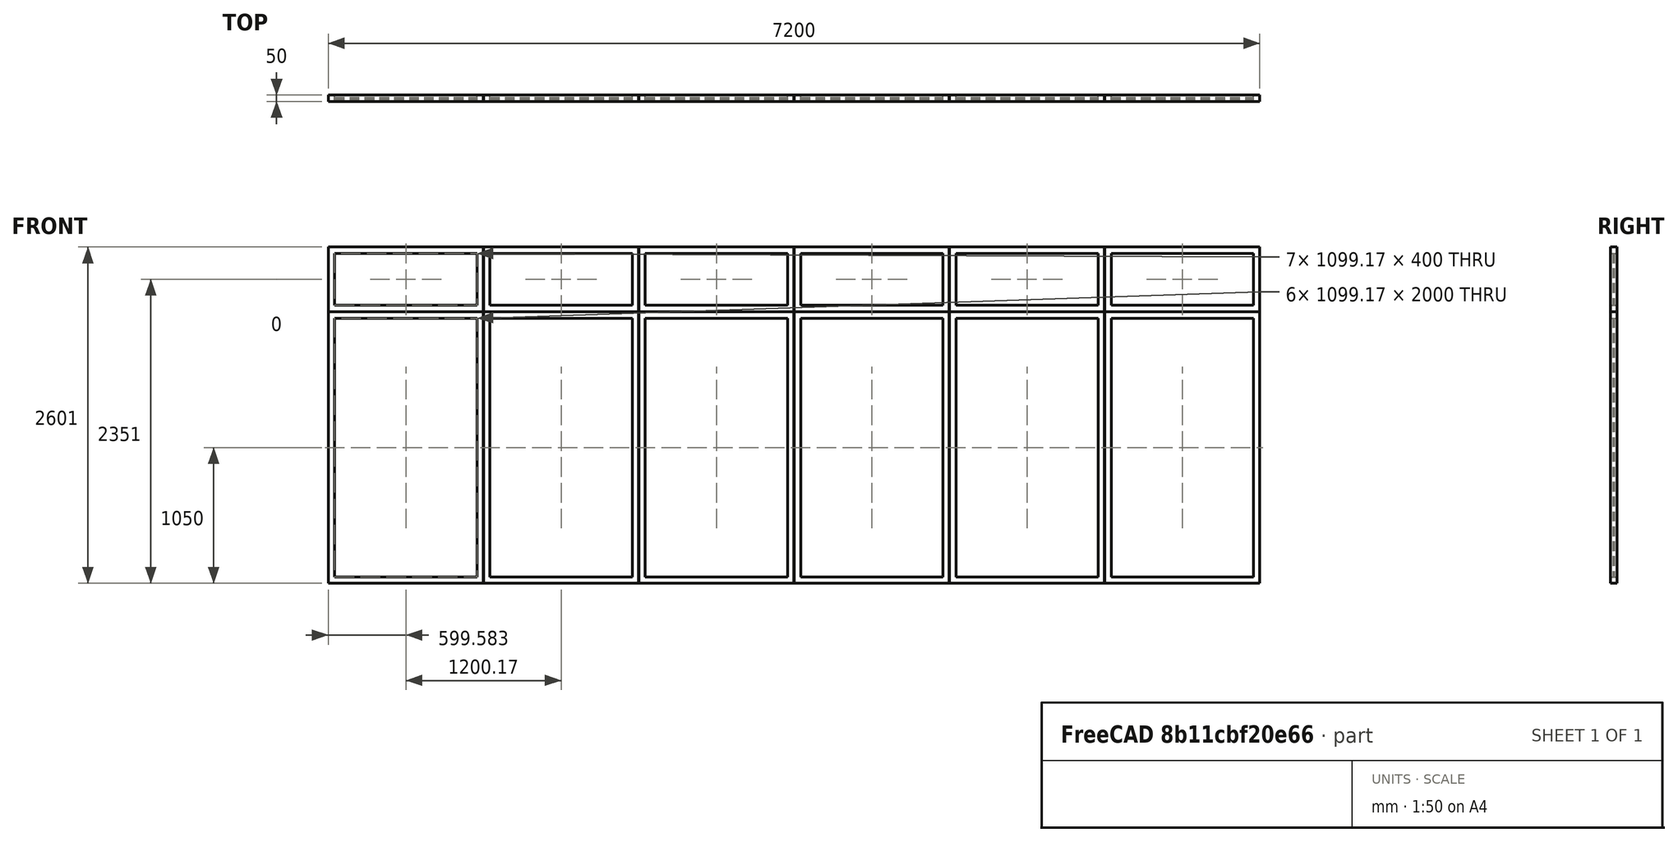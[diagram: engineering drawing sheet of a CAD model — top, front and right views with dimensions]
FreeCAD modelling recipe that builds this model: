
FCSTD DOCUMENT  (FreeCAD 0.16R6704 (Git))
Label: 6 frame modules
License: CreativeCommons Attribution
LicenseURL: http://creativecommons.org/licenses/by/4.0/
objects: Sketcher::SketchObject×1, Part::FeaturePython×1
note: 2 computed .brp shape members not serialized (recipe doc carries the construction recipe); baked Part::Feature solids carry a one-line shape summary decoded from their .brp

FEATURE [Sketcher::SketchObject] Sketch189
  Placement = pos=(0,0,0) rot=(1,0,0;1.5708rad)
  sketch-geometry (125):
    g0: LineSegment StartX=-2 StartY=-2 StartZ=0 EndX=7202 EndY=-2 EndZ=0
    g1: LineSegment StartX=7202 StartY=-2 StartZ=0 EndX=7202 EndY=2603 EndZ=0
    g2: LineSegment StartX=7202 StartY=2603 StartZ=0 EndX=-2 EndY=2603 EndZ=0
    g3: LineSegment StartX=-2 StartY=2603 StartZ=0 EndX=-2 EndY=-2 EndZ=0
    g4: LineSegment StartX=0 StartY=2601 StartZ=0 EndX=1199.17 EndY=2601 EndZ=0
    g5: LineSegment StartX=1199.17 StartY=2601 StartZ=0 EndX=1199.17 EndY=2101 EndZ=0
    g6: LineSegment StartX=1199.17 StartY=2101 StartZ=0 EndX=0 EndY=2101 EndZ=0
    g7: LineSegment StartX=0 StartY=2101 StartZ=0 EndX=0 EndY=2601 EndZ=0
    g8: LineSegment StartX=50 StartY=2551 StartZ=0 EndX=1149.17 EndY=2551 EndZ=0
    g9: LineSegment StartX=1149.17 StartY=2551 StartZ=0 EndX=1149.17 EndY=2151 EndZ=0
    g10: LineSegment StartX=1149.17 StartY=2151 StartZ=0 EndX=50 EndY=2151 EndZ=0
    g11: LineSegment StartX=50 StartY=2151 StartZ=0 EndX=50 EndY=2551 EndZ=0
    g12: LineSegment StartX=0 StartY=2100 StartZ=0 EndX=1199.17 EndY=2100 EndZ=0
    g13: LineSegment StartX=1199.17 StartY=2100 StartZ=0 EndX=1199.17 EndY=0 EndZ=0
    g14: LineSegment StartX=1199.17 StartY=0 StartZ=0 EndX=0 EndY=0 EndZ=0
    g15: LineSegment StartX=0 StartY=0 StartZ=0 EndX=0 EndY=2100 EndZ=0
    g16: LineSegment StartX=50 StartY=2050 StartZ=0 EndX=1149.17 EndY=2050 EndZ=0
    g17: LineSegment StartX=1149.17 StartY=2050 StartZ=0 EndX=1149.17 EndY=50 EndZ=0
    g18: LineSegment StartX=1149.17 StartY=50 StartZ=0 EndX=50 EndY=50 EndZ=0
    g19: LineSegment StartX=50 StartY=50 StartZ=0 EndX=50 EndY=2050 EndZ=0
    g20: LineSegment StartX=-1 StartY=2602 StartZ=0 EndX=7201 EndY=2602 EndZ=0
    g21: LineSegment StartX=7201 StartY=2602 StartZ=0 EndX=7201 EndY=-1 EndZ=0
    g22: LineSegment StartX=7201 StartY=-1 StartZ=0 EndX=-1 EndY=-1 EndZ=0
    g23: LineSegment StartX=-1 StartY=-1 StartZ=0 EndX=-1 EndY=2602 EndZ=0
    g24: LineSegment StartX=1200.17 StartY=2601 StartZ=0 EndX=2399.33 EndY=2601 EndZ=0
    g25: LineSegment StartX=2399.33 StartY=2601 StartZ=0 EndX=2399.33 EndY=2101 EndZ=0
    g26: LineSegment StartX=2399.33 StartY=2101 StartZ=0 EndX=1200.17 EndY=2101 EndZ=0
    g27: LineSegment StartX=1200.17 StartY=2101 StartZ=0 EndX=1200.17 EndY=2601 EndZ=0
    g28: LineSegment StartX=1250.17 StartY=2551 StartZ=0 EndX=2349.33 EndY=2551 EndZ=0
    g29: LineSegment StartX=2349.33 StartY=2551 StartZ=0 EndX=2349.33 EndY=2151 EndZ=0
    g30: LineSegment StartX=2349.33 StartY=2151 StartZ=0 EndX=1250.17 EndY=2151 EndZ=0
    g31: LineSegment StartX=1250.17 StartY=2151 StartZ=0 EndX=1250.17 EndY=2551 EndZ=0
    g32: LineSegment StartX=1200.17 StartY=2100 StartZ=0 EndX=2399.33 EndY=2100 EndZ=0
    g33: LineSegment StartX=2399.33 StartY=2100 StartZ=0 EndX=2399.33 EndY=0 EndZ=0
    g34: LineSegment StartX=2399.33 StartY=0 StartZ=0 EndX=1200.17 EndY=0 EndZ=0
    g35: LineSegment StartX=1200.17 StartY=0 StartZ=0 EndX=1200.17 EndY=2100 EndZ=0
    g36: LineSegment StartX=1250.17 StartY=2050 StartZ=0 EndX=2349.33 EndY=2050 EndZ=0
    g37: LineSegment StartX=2349.33 StartY=2050 StartZ=0 EndX=2349.33 EndY=50 EndZ=0
    g38: LineSegment StartX=2349.33 StartY=50 StartZ=0 EndX=1250.17 EndY=50 EndZ=0
    g39: LineSegment StartX=1250.17 StartY=50 StartZ=0 EndX=1250.17 EndY=2050 EndZ=0
    g40: LineSegment [constr] StartX=0 StartY=2601 StartZ=0 EndX=1200.17 EndY=2601 EndZ=0
    g41: LineSegment StartX=2400.33 StartY=2601 StartZ=0 EndX=3599.5 EndY=2601 EndZ=0
    g42: LineSegment StartX=3599.5 StartY=2601 StartZ=0 EndX=3599.5 EndY=2101 EndZ=0
    g43: LineSegment StartX=3599.5 StartY=2101 StartZ=0 EndX=2400.33 EndY=2101 EndZ=0
    g44: LineSegment StartX=2400.33 StartY=2101 StartZ=0 EndX=2400.33 EndY=2601 EndZ=0
    g45: LineSegment StartX=2450.33 StartY=2551 StartZ=0 EndX=3549.5 EndY=2551 EndZ=0
    g46: LineSegment StartX=3549.5 StartY=2551 StartZ=0 EndX=3549.5 EndY=2151 EndZ=0
    g47: LineSegment StartX=3549.5 StartY=2151 StartZ=0 EndX=2450.33 EndY=2151 EndZ=0
    g48: LineSegment StartX=2450.33 StartY=2151 StartZ=0 EndX=2450.33 EndY=2551 EndZ=0
    g49: LineSegment StartX=2400.33 StartY=2100 StartZ=0 EndX=3599.5 EndY=2100 EndZ=0
    g50: LineSegment StartX=3599.5 StartY=2100 StartZ=0 EndX=3599.5 EndY=0 EndZ=0
    g51: LineSegment StartX=3599.5 StartY=0 StartZ=0 EndX=2400.33 EndY=0 EndZ=0
    g52: LineSegment StartX=2400.33 StartY=0 StartZ=0 EndX=2400.33 EndY=2100 EndZ=0
    g53: LineSegment StartX=2450.33 StartY=2050 StartZ=0 EndX=3549.5 EndY=2050 EndZ=0
    g54: LineSegment StartX=3549.5 StartY=2050 StartZ=0 EndX=3549.5 EndY=50 EndZ=0
    g55: LineSegment StartX=3549.5 StartY=50 StartZ=0 EndX=2450.33 EndY=50 EndZ=0
    g56: LineSegment StartX=2450.33 StartY=50 StartZ=0 EndX=2450.33 EndY=2050 EndZ=0
    g57: LineSegment [constr] StartX=1200.17 StartY=2601 StartZ=0 EndX=2400.33 EndY=2601 EndZ=0
    g58: LineSegment StartX=3600.5 StartY=2601 StartZ=0 EndX=4799.67 EndY=2601 EndZ=0
    g59: LineSegment StartX=4799.67 StartY=2601 StartZ=0 EndX=4799.67 EndY=2101 EndZ=0
    g60: LineSegment StartX=4799.67 StartY=2101 StartZ=0 EndX=3600.5 EndY=2101 EndZ=0
    g61: LineSegment StartX=3600.5 StartY=2101 StartZ=0 EndX=3600.5 EndY=2601 EndZ=0
    g62: LineSegment StartX=3650.5 StartY=2551 StartZ=0 EndX=4749.67 EndY=2551 EndZ=0
    g63: LineSegment StartX=4749.67 StartY=2551 StartZ=0 EndX=4749.67 EndY=2151 EndZ=0
    g64: LineSegment StartX=4749.67 StartY=2151 StartZ=0 EndX=3650.5 EndY=2151 EndZ=0
    g65: LineSegment StartX=3650.5 StartY=2151 StartZ=0 EndX=3650.5 EndY=2551 EndZ=0
    g66: LineSegment StartX=3600.5 StartY=2100 StartZ=0 EndX=4799.67 EndY=2100 EndZ=0
    g67: LineSegment StartX=4799.67 StartY=2100 StartZ=0 EndX=4799.67 EndY=0 EndZ=0
    g68: LineSegment StartX=4799.67 StartY=0 StartZ=0 EndX=3600.5 EndY=0 EndZ=0
    g69: LineSegment StartX=3600.5 StartY=0 StartZ=0 EndX=3600.5 EndY=2100 EndZ=0
    g70: LineSegment StartX=3650.5 StartY=2050 StartZ=0 EndX=4749.67 EndY=2050 EndZ=0
    g71: LineSegment StartX=4749.67 StartY=2050 StartZ=0 EndX=4749.67 EndY=50 EndZ=0
    g72: LineSegment StartX=4749.67 StartY=50 StartZ=0 EndX=3650.5 EndY=50 EndZ=0
    g73: LineSegment StartX=3650.5 StartY=50 StartZ=0 EndX=3650.5 EndY=2050 EndZ=0
    g74: LineSegment [constr] StartX=2400.33 StartY=2601 StartZ=0 EndX=3600.5 EndY=2601 EndZ=0
    g75: LineSegment StartX=4800.67 StartY=2601 StartZ=0 EndX=5999.83 EndY=2601 EndZ=0
    g76: LineSegment StartX=5999.83 StartY=2601 StartZ=0 EndX=5999.83 EndY=2101 EndZ=0
    g77: LineSegment StartX=5999.83 StartY=2101 StartZ=0 EndX=4800.67 EndY=2101 EndZ=0
    g78: LineSegment StartX=4800.67 StartY=2101 StartZ=0 EndX=4800.67 EndY=2601 EndZ=0
    g79: LineSegment StartX=4850.67 StartY=2551 StartZ=0 EndX=5949.83 EndY=2551 EndZ=0
    g80: LineSegment StartX=5949.83 StartY=2551 StartZ=0 EndX=5949.83 EndY=2151 EndZ=0
    g81: LineSegment StartX=5949.83 StartY=2151 StartZ=0 EndX=4850.67 EndY=2151 EndZ=0
    g82: LineSegment StartX=4850.67 StartY=2151 StartZ=0 EndX=4850.67 EndY=2551 EndZ=0
    g83: LineSegment StartX=4800.67 StartY=2100 StartZ=0 EndX=5999.83 EndY=2100 EndZ=0
    g84: LineSegment StartX=5999.83 StartY=2100 StartZ=0 EndX=5999.83 EndY=0 EndZ=0
    g85: LineSegment StartX=5999.83 StartY=0 StartZ=0 EndX=4800.67 EndY=0 EndZ=0
    g86: LineSegment StartX=4800.67 StartY=0 StartZ=0 EndX=4800.67 EndY=2100 EndZ=0
    g87: LineSegment StartX=4850.67 StartY=2050 StartZ=0 EndX=5949.83 EndY=2050 EndZ=0
    g88: LineSegment StartX=5949.83 StartY=2050 StartZ=0 EndX=5949.83 EndY=50 EndZ=0
    g89: LineSegment StartX=5949.83 StartY=50 StartZ=0 EndX=4850.67 EndY=50 EndZ=0
    g90: LineSegment StartX=4850.67 StartY=50 StartZ=0 EndX=4850.67 EndY=2050 EndZ=0
    g91: LineSegment [constr] StartX=3600.5 StartY=2601 StartZ=0 EndX=4800.67 EndY=2601 EndZ=0
    g92: LineSegment StartX=6000.83 StartY=2601 StartZ=0 EndX=7200 EndY=2601 EndZ=0
    g93: LineSegment StartX=7200 StartY=2601 StartZ=0 EndX=7200 EndY=2101 EndZ=0
    g94: LineSegment StartX=7200 StartY=2101 StartZ=0 EndX=6000.83 EndY=2101 EndZ=0
    g95: LineSegment StartX=6000.83 StartY=2101 StartZ=0 EndX=6000.83 EndY=2601 EndZ=0
    g96: LineSegment StartX=6050.83 StartY=2551 StartZ=0 EndX=7150 EndY=2551 EndZ=0
    g97: LineSegment StartX=7150 StartY=2551 StartZ=0 EndX=7150 EndY=2151 EndZ=0
    g98: LineSegment StartX=7150 StartY=2151 StartZ=0 EndX=6050.83 EndY=2151 EndZ=0
    g99: LineSegment StartX=6050.83 StartY=2151 StartZ=0 EndX=6050.83 EndY=2551 EndZ=0
    g100: LineSegment StartX=6000.83 StartY=2100 StartZ=0 EndX=7200 EndY=2100 EndZ=0
    g101: LineSegment StartX=7200 StartY=2100 StartZ=0 EndX=7200 EndY=0 EndZ=0
    g102: LineSegment StartX=7200 StartY=0 StartZ=0 EndX=6000.83 EndY=0 EndZ=0
    g103: LineSegment StartX=6000.83 StartY=0 StartZ=0 EndX=6000.83 EndY=2100 EndZ=0
    g104: LineSegment StartX=6050.83 StartY=2050 StartZ=0 EndX=7150 EndY=2050 EndZ=0
    g105: LineSegment StartX=7150 StartY=2050 StartZ=0 EndX=7150 EndY=50 EndZ=0
    g106: LineSegment StartX=7150 StartY=50 StartZ=0 EndX=6050.83 EndY=50 EndZ=0
    g107: LineSegment StartX=6050.83 StartY=50 StartZ=0 EndX=6050.83 EndY=2050 EndZ=0
    g108: LineSegment [constr] StartX=4800.67 StartY=2601 StartZ=0 EndX=6000.83 EndY=2601 EndZ=0
    g109: LineSegment [constr] StartX=205.779 StartY=2601 StartZ=0 EndX=205.779 EndY=2551 EndZ=0
    g110: LineSegment [constr] StartX=7150 StartY=2541.61 StartZ=0 EndX=7200 EndY=2541.61 EndZ=0
    g111: LineSegment [constr] StartX=88 StartY=50 StartZ=0 EndX=88 EndY=0 EndZ=0
    g112: LineSegment [constr] StartX=0 StartY=2427.79 StartZ=0 EndX=50 EndY=2427.79 EndZ=0
    g113: LineSegment [constr] StartX=96.74 StartY=2100 StartZ=0 EndX=96.74 EndY=2050 EndZ=0
    g114: LineSegment [constr] StartX=1149.17 StartY=2536 StartZ=0 EndX=1199.17 EndY=2536 EndZ=0
    g115: LineSegment [constr] StartX=1200.17 StartY=2541.5 StartZ=0 EndX=1250.17 EndY=2541.5 EndZ=0
    g116: LineSegment [constr] StartX=2349.33 StartY=2501 StartZ=0 EndX=2399.33 EndY=2501 EndZ=0
    g117: LineSegment [constr] StartX=2400.33 StartY=2503.79 StartZ=0 EndX=2450.33 EndY=2503.79 EndZ=0
    g118: LineSegment [constr] StartX=3549.5 StartY=2540.22 StartZ=0 EndX=3599.5 EndY=2540.22 EndZ=0
    g119: LineSegment [constr] StartX=3600.5 StartY=2535.71 StartZ=0 EndX=3650.5 EndY=2535.71 EndZ=0
    g120: LineSegment [constr] StartX=4749.67 StartY=2525 StartZ=0 EndX=4799.67 EndY=2525 EndZ=0
    g121: LineSegment [constr] StartX=4800.67 StartY=2526.63 StartZ=0 EndX=4850.67 EndY=2526.63 EndZ=0
    g122: LineSegment [constr] StartX=5949.83 StartY=2492.37 StartZ=0 EndX=5999.83 EndY=2492.37 EndZ=0
    g123: LineSegment [constr] StartX=6000.83 StartY=2485 StartZ=0 EndX=6050.83 EndY=2485 EndZ=0
    g124: LineSegment [constr] StartX=157.804 StartY=2151 StartZ=0 EndX=157.804 EndY=2101 EndZ=0
  constraints (369):
    c: Coincident(g0,g1)
    c: Coincident(g1,g2)
    c: Coincident(g2,g3)
    c: Coincident(g3,g0)
    c: Horizontal(g0)
    c: Horizontal(g2)
    c: Vertical(g1)
    c: Vertical(g3)
    c: Coincident(g4,g5)
    c: Coincident(g5,g6)
    c: Coincident(g6,g7)
    c: Coincident(g7,g4)
    c: Horizontal(g4)
    c: Horizontal(g6)
    c: Vertical(g5)
    c: Vertical(g7)
    c: Coincident(g8,g9)
    c: Coincident(g9,g10)
    c: Coincident(g10,g11)
    c: Coincident(g11,g8)
    c: Horizontal(g8)
    c: Horizontal(g10)
    c: Vertical(g9)
    c: Vertical(g11)
    c: Coincident(g12,g13)
    c: Coincident(g13,g14)
    c: Coincident(g14,g15)
    c: Coincident(g15,g12)
    c: Horizontal(g12)
    c: Horizontal(g14)
    c: Vertical(g13)
    c: Vertical(g15)
    c: Coincident(g16,g17)
    c: Coincident(g17,g18)
    c: Coincident(g18,g19)
    c: Coincident(g19,g16)
    c: Horizontal(g16)
    c: Horizontal(g18)
    c: Vertical(g17)
    c: Vertical(g19)
    c: Coincident(g20,g21)
    c: Coincident(g21,g22)
    c: Coincident(g22,g23)
    c: Coincident(g23,g20)
    c: Horizontal(g20)
    c: Horizontal(g22)
    c: Vertical(g21)
    c: Vertical(g23)
    c: DistanceX(g2,g20) = 1
    c: DistanceY(g20,g2) = 1
    c: DistanceX(g21,g0) = 1
    c: DistanceY(g0,g21) = 1
    c: DistanceX(g20,g4) = 1
    c: DistanceY(g4,g20) = 1
    c: DistanceX(g22,g14) = 1
    c: DistanceY(g22,g14) = 1
    c: DistanceY(g12,g6) = 1
    c: DistanceX(g4,g8) = 50  'Montantes'
    c: Coincident(g14,g-1)  'Constraint59'
    c: DistanceY(g-1,g12) = 2100  'Altura do módulo inferior'
    c: DistanceY(g6,g4) = 500  'Altura do módulo superior'
    c: Coincident(g24,g25)
    c: Coincident(g25,g26)
    c: Coincident(g26,g27)
    c: Coincident(g27,g24)
    c: Horizontal(g24)
    c: Horizontal(g26)
    c: Vertical(g25)
    c: Vertical(g27)
    c: Coincident(g28,g29)
    c: Coincident(g29,g30)
    c: Coincident(g30,g31)
    c: Coincident(g31,g28)
    c: Horizontal(g28)
    c: Horizontal(g30)
    c: Vertical(g29)
    c: Vertical(g31)
    c: Coincident(g32,g33)
    c: Coincident(g33,g34)
    c: Coincident(g34,g35)
    c: Coincident(g35,g32)
    c: Horizontal(g32)
    c: Horizontal(g34)
    c: Vertical(g33)
    c: Vertical(g35)
    c: Coincident(g36,g37)
    c: Coincident(g37,g38)
    c: Coincident(g38,g39)
    c: Coincident(g39,g36)
    c: Horizontal(g36)
    c: Horizontal(g38)
    c: Vertical(g37)
    c: Vertical(g39)
    c: DistanceY(g32,g26) = 1
    c: Equal(g4,g24) = 1199
    c: Coincident(g4,g40)
    c: Coincident(g24,g40)
    c: Angle(g40) = 0
    c: Coincident(g41,g42)
    c: Coincident(g42,g43)
    c: Coincident(g43,g44)
    c: Coincident(g44,g41)
    c: Horizontal(g41)
    c: Horizontal(g43)
    c: Vertical(g42)
    c: Vertical(g44)
    c: Coincident(g45,g46)
    c: Coincident(g46,g47)
    c: Coincident(g47,g48)
    c: Coincident(g48,g45)
    c: Horizontal(g45)
    c: Horizontal(g47)
    c: Vertical(g46)
    c: Vertical(g48)
    c: Coincident(g49,g50)
    c: Coincident(g50,g51)
    c: Coincident(g51,g52)
    c: Coincident(g52,g49)
    c: Horizontal(g49)
    c: Horizontal(g51)
    c: Vertical(g50)
    c: Vertical(g52)
    c: Coincident(g53,g54)
    c: Coincident(g54,g55)
    c: Coincident(g55,g56)
    c: Coincident(g56,g53)
    c: Horizontal(g53)
    c: Horizontal(g55)
    c: Vertical(g54)
    c: Vertical(g56)
    c: DistanceY(g49,g43) = 1
    c: Equal(g4,g41) = 1199
    c: Coincident(g24,g57)
    c: Coincident(g41,g57)
    c: Equal(g40,g57)
    c: Parallel(g57,g40)
    c: Coincident(g58,g59)
    c: Coincident(g59,g60)
    c: Coincident(g60,g61)
    c: Coincident(g61,g58)
    c: Horizontal(g58)
    c: Horizontal(g60)
    c: Vertical(g59)
    c: Vertical(g61)
    c: Coincident(g62,g63)
    c: Coincident(g63,g64)
    c: Coincident(g64,g65)
    c: Coincident(g65,g62)
    c: Horizontal(g62)
    c: Horizontal(g64)
    c: Vertical(g63)
    c: Vertical(g65)
    c: Coincident(g66,g67)
    c: Coincident(g67,g68)
    c: Coincident(g68,g69)
    c: Coincident(g69,g66)
    c: Horizontal(g66)
    c: Horizontal(g68)
    c: Vertical(g67)
    c: Vertical(g69)
    c: Coincident(g70,g71)
    c: Coincident(g71,g72)
    c: Coincident(g72,g73)
    c: Coincident(g73,g70)
    c: Horizontal(g70)
    c: Horizontal(g72)
    c: Vertical(g71)
    c: Vertical(g73)
    c: DistanceY(g66,g60) = 1
    c: Equal(g4,g58) = 1199
    c: Coincident(g41,g74)
    c: Coincident(g58,g74)
    c: Equal(g40,g74)
    c: Parallel(g74,g40)
    c: Coincident(g75,g76)
    c: Coincident(g76,g77)
    c: Coincident(g77,g78)
    c: Coincident(g78,g75)
    c: Horizontal(g75)
    c: Horizontal(g77)
    c: Vertical(g76)
    c: Vertical(g78)
    c: Coincident(g79,g80)
    c: Coincident(g80,g81)
    c: Coincident(g81,g82)
    c: Coincident(g82,g79)
    c: Horizontal(g79)
    c: Horizontal(g81)
    c: Vertical(g80)
    c: Vertical(g82)
    c: Coincident(g83,g84)
    c: Coincident(g84,g85)
    c: Coincident(g85,g86)
    c: Coincident(g86,g83)
    c: Horizontal(g83)
    c: Horizontal(g85)
    c: Vertical(g84)
    c: Vertical(g86)
    c: Coincident(g87,g88)
    c: Coincident(g88,g89)
    c: Coincident(g89,g90)
    c: Coincident(g90,g87)
    c: Horizontal(g87)
    c: Horizontal(g89)
    c: Vertical(g88)
    c: Vertical(g90)
    c: DistanceY(g83,g77) = 1
    c: Equal(g4,g75) = 1199
    c: Coincident(g58,g91)
    c: Coincident(g75,g91)
    c: Equal(g40,g91)
    c: Parallel(g91,g40)
    c: Coincident(g92,g93)
    c: Coincident(g93,g94)
    c: Coincident(g94,g95)
    c: Coincident(g95,g92)
    c: Horizontal(g92)
    c: Horizontal(g94)
    c: Vertical(g93)
    c: Vertical(g95)
    c: Coincident(g96,g97)
    c: Coincident(g97,g98)
    c: Coincident(g98,g99)
    c: Coincident(g99,g96)
    c: Horizontal(g96)
    c: Horizontal(g98)
    c: Vertical(g97)
    c: Vertical(g99)
    c: Coincident(g100,g101)
    c: Coincident(g101,g102)
    c: Coincident(g102,g103)
    c: Coincident(g103,g100)
    c: Horizontal(g100)
    c: Horizontal(g102)
    c: Vertical(g101)
    c: Vertical(g103)
    c: Coincident(g104,g105)
    c: Coincident(g105,g106)
    c: Coincident(g106,g107)
    c: Coincident(g107,g104)
    c: Horizontal(g104)
    c: Horizontal(g106)
    c: Vertical(g105)
    c: Vertical(g107)
    c: DistanceY(g100,g94) = 1
    c: Equal(g4,g92) = 1199
    c: Coincident(g75,g108)
    c: Coincident(g92,g108)
    c: Equal(g40,g108)
    c: Parallel(g108,g40)
    c: DistanceX(g26,g32) = 0
    c: DistanceX(g25,g32) = 0
    c: DistanceX(g43,g49) = 0
    c: DistanceX(g42,g49) = 0
    c: DistanceX(g60,g66) = 0
    c: DistanceX(g59,g66) = 0
    c: DistanceX(g77,g83) = 0
    c: DistanceX(g76,g83) = 0
    c: DistanceX(g94,g100) = 0
    c: DistanceX(g93,g100) = 0
    c: PointOnObject(g109,g8)
    c: PointOnObject(g109,g4)
    c: PointOnObject(g110,g97)
    c: PointOnObject(g110,g93)
    c: DistanceY(g80,g98) = 0
    c: DistanceX(g97,g104) = 0
    c: DistanceY(g87,g104) = 0
    c: DistanceX(g80,g87) = 0
    c: DistanceX(g98,g104) = 0
    c: DistanceX(g76,g94) = 1
    c: DistanceY(g63,g81) = 0
    c: DistanceX(g63,g70) = 0
    c: DistanceY(g70,g87) = 0
    c: DistanceX(g81,g87) = 0
    c: DistanceY(g46,g64) = 0
    c: DistanceY(g53,g70) = 0
    c: DistanceX(g46,g53) = 0
    c: DistanceX(g64,g70) = 0
    c: DistanceY(g29,g47) = 0
    c: DistanceX(g29,g36) = 0
    c: DistanceY(g36,g53) = 0
    c: DistanceX(g47,g53) = 0
    c: DistanceX(g5,g12) = 0
    c: DistanceY(g9,g30) = 0
    c: DistanceY(g16,g36) = 0
    c: DistanceX(g9,g16) = 0
    c: DistanceX(g30,g36) = 0
    c: DistanceX(g10,g16) = 0
    c: PointOnObject(g111,g18)
    c: PointOnObject(g111,g14)
    c: DistanceY(g17,g38) = 0
    c: DistanceY(g13,g34) = 0
    c: DistanceY(g37,g55) = 0
    c: DistanceY(g33,g51) = 0
    c: DistanceY(g54,g72) = 0
    c: DistanceY(g50,g68) = 0
    c: DistanceY(g71,g89) = 0
    c: DistanceY(g67,g85) = 0
    c: DistanceY(g88,g106) = 0
    c: DistanceY(g84,g102) = 0
    c: PointOnObject(g112,g7)
    c: PointOnObject(g112,g11)
    c: Horizontal(g112)
    c: PointOnObject(g113,g12)
    c: PointOnObject(g113,g16)
    c: PointOnObject(g114,g9)
    c: PointOnObject(g114,g5)
    c: PointOnObject(g115,g27)
    c: PointOnObject(g115,g31)
    c: PointOnObject(g116,g29)
    c: PointOnObject(g116,g25)
    c: PointOnObject(g117,g44)
    c: PointOnObject(g117,g48)
    c: PointOnObject(g118,g46)
    c: PointOnObject(g118,g42)
    c: PointOnObject(g119,g61)
    c: PointOnObject(g119,g65)
    c: PointOnObject(g120,g63)
    c: PointOnObject(g120,g59)
    c: PointOnObject(g121,g78)
    c: PointOnObject(g121,g82)
    c: PointOnObject(g122,g80)
    c: PointOnObject(g122,g76)
    c: PointOnObject(g123,g95)
    c: PointOnObject(g123,g99)
    c: DistanceY(g8,g28) = 0
    c: DistanceY(g28,g45) = 0
    c: DistanceY(g45,g62) = 0
    c: DistanceY(g79,g62) = 0
    c: DistanceY(g96,g79) = 0
    c: PointOnObject(g124,g10)
    c: PointOnObject(g124,g6)
    c: DistanceX(g-1,g101) = 7200  'Largura do vão'
    c: Equal(g109,g112)  'Constraint348'
    c: Equal(g112,g124)  'Constraint347'
    c: Equal(g124,g113)  'Constraint346'
    c: Equal(g113,g114)  'Constraint345'
    c: Equal(g114,g115)  'Constraint344'
    c: Equal(g115,g116)  'Constraint343'
    c: Equal(g116,g117)  'Constraint342'
    c: Equal(g117,g118)  'Constraint341'
    c: Equal(g118,g119)
    c: Equal(g119,g120)
    c: Equal(g120,g121)
    c: Equal(g121,g122)
    c: Equal(g122,g123)
    c: Equal(g123,g110)
    c: Equal(g110,g111)
    c: DistanceY(g26,g5) = 0
    c: DistanceY(g43,g25) = 0
    c: DistanceY(g60,g42) = 0
    c: DistanceY(g77,g59) = 0
    c: DistanceY(g94,g76) = 0
    c: DistanceX(g101,g21) = 1
    c: Angle(g109) = -1.5708
    c: Angle(g124) = -1.5708
    c: Angle(g113) = -1.5708
    c: Angle(g111) = -1.5708
    c: Angle(g110) = 0
    c: Angle(g114) = 0
    c: Angle(g115) = 0
    c: Angle(g116) = 0
    c: Angle(g117) = 0
    c: Angle(g118) = 0
    c: Angle(g119) = 0
    c: Angle(g120) = 0
    c: Angle(g121) = 0
    c: Angle(g122) = 0
    c: Angle(g123) = 0
FEATURE [Part::FeaturePython] Window119  label="6 frame modules"  # WARN: FeaturePython — macro-defined, semantics opaque (R4)
  Base = -> Sketch189
  Height = 0
  HoleDepth = 0
  MoveWithHost = true
  Normal = (0,1,0)
  Preset = 0
  Role = 0
  Width = 0
  WindowParts = CAIXILHO 1 | Frame | Wire1,Wire2 | 50.0 | 0.0 | VIDRO1 | Glass panel | Wire2 | 10.0 | 20.0 | CAIXILHO 2 | Frame | Wire3,Wire4 | 50.0 | 0.0 | VIDRO 2 | Glass panel | Wire4 | 10.0 | 20.0 | CAIXILHO 3 | Frame | Wire6,Wire7 | 50.0 | 0.0 | VIDRO 3 | Glass panel | Wire7 | 10.0 | 20.0 | CAIXILHO 4 | Frame | Wire8,Wire9 | 50.0 | 0.0 | VIDRO 4 | Glass panel | Wire9 | 10.0 | 20.0 | CAIXILHO 5 | Frame | Wire10,Wire11 | 50.0 | 0.0 | VIDRO 5 | Glass panel | Wire11 | 10.0 | 20.0 | CAIXILHO 6 | Frame | Wire12,Wire13 | 50.0 | 0.0 | VIDRO 6 | Glass panel | Wire13 | 10.0 | 20.0 | CAIXILHO 7 | Frame | Wire14,Wire15 | 50.0 | 0.0 | VIDRO 7 | Glass panel | Wire15 | 10.0 | 20.0 | CAIXILHO 8 | Frame | Wire16,Wire17 | 50.0 | 0.0 | VIDRO 8 | Glass panel | Wire17 | 10.0 | 20.0 | CAIXILHO 9 | Solid panel | Wire18,Wire19 | 50.0 | 0.0 | VIDRO 9 | Glass panel | Wire19 | 10.0 | 20.0 | CAIXILHO 10 | Frame | Wire20,Wire21 | 50.0 | 0.0 | VIDRO 10 | Glass panel | Wire21 | 10.0 | 20.0 | CAIXILHO 11 | Frame | Wire22,Wire23 | 50.0 | 0.0 | VIDRO 11 | Glass panel | Wire23 | 10.0 | 20.0 | CAIXILHO 12 | Frame | Wire24,Wire25 | 50.0 | 0.0 | VIDRO 12 | Glass panel | Wire25 | 10.0 | 20.0 | CAIXILHO 01 | Frame | Wire1,Wire2 | 50.0 | 0.0
